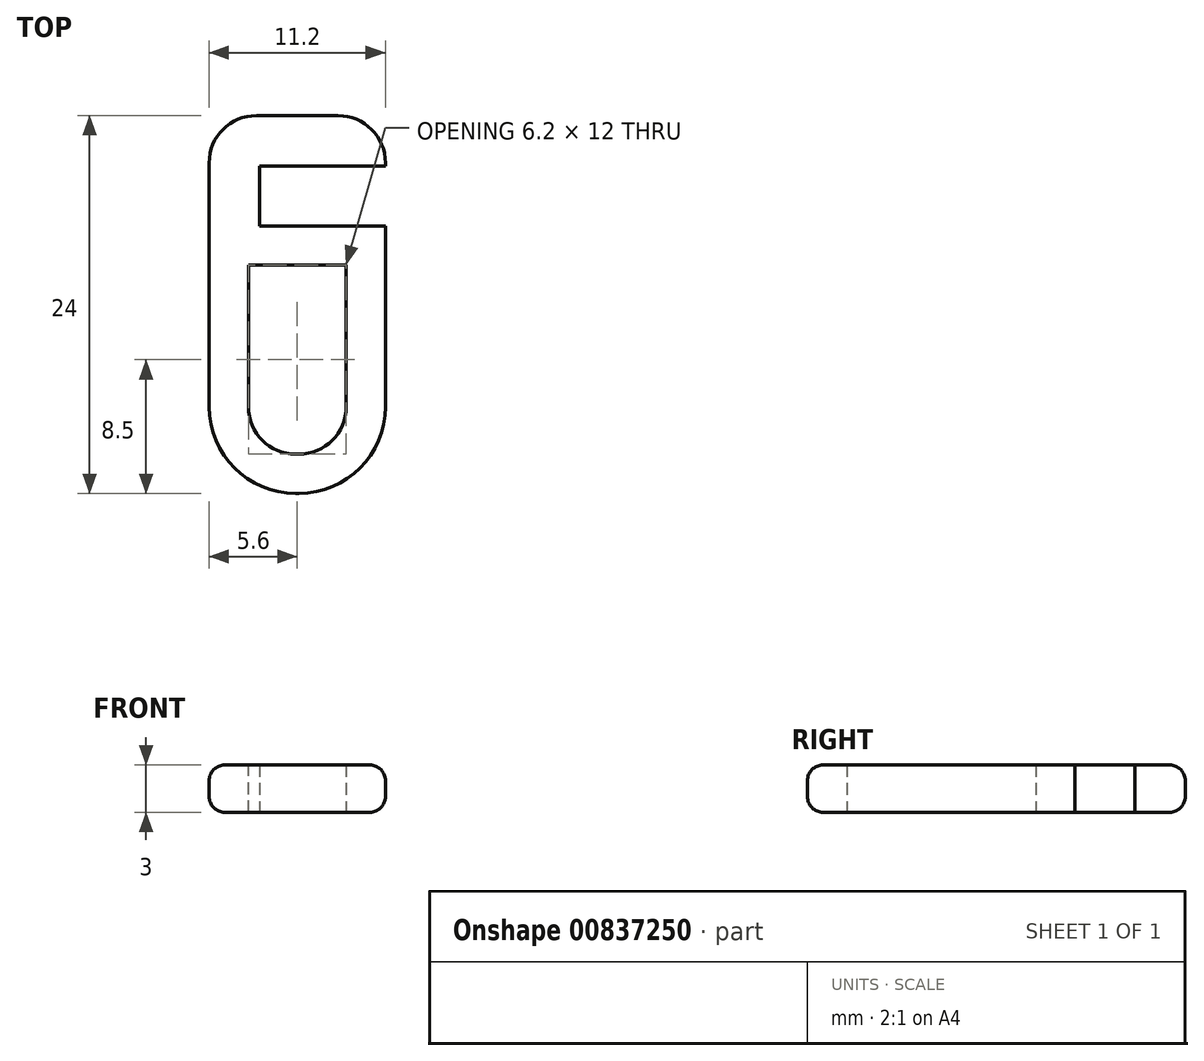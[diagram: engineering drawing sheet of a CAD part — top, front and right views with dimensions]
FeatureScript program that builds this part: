
annotation { "Feature Type Name" : "Feature", "Feature Type Description" : "" }
export const myFeature = defineFeature(function(context is Context, id is Id, definition is map)
    precondition{}
    {
        {
            var Q0;
            Q0=qCreatedBy(makeId("Top.planeOp"),FACE);
            var sketch = newSketch(context, id + "F0", { "sketchPlane" : qUnion([Q0])});
            skLineSegment(sketch, "E0", {"start": v(0, 0) * mm, "end": v(0, -17) * mm, "construction": true});
            skLineSegment(sketch, "E1", {"start": v(0, 0) * mm, "end": v(0, 3.8) * mm, "construction": true});
            skLineSegment(sketch, "E2", {"start": v(0, 18.8) * mm, "end": v(0, 3.8) * mm, "construction": true});
            skLineSegment(sketch, "E3", {"start": v(0, 0) * mm, "end": v(8, 0) * mm, "construction": true});
            skLineSegment(sketch, "E4.bottom", {"start": v(8, 0) * mm, "end": v(-3.2, 0) * mm});
            skLineSegment(sketch, "E4.top", {"start": v(8, -17) * mm, "end": v(-3.2, -17) * mm});
            skLineSegment(sketch, "E4.left", {"start": v(8, 0) * mm, "end": v(8, -17) * mm});
            skLineSegment(sketch, "E4.right", {"start": v(-3.2, 0) * mm, "end": v(-3.2, -17) * mm});
            skLineSegment(sketch, "E5.bottom", {"start": v(-3.2, 3.8) * mm, "end": v(0, 3.8) * mm});
            skLineSegment(sketch, "E5.top", {"start": v(-3.2, 0) * mm, "end": v(0, 0) * mm});
            skLineSegment(sketch, "E5.left", {"start": v(-3.2, 3.8) * mm, "end": v(-3.2, 0) * mm});
            skLineSegment(sketch, "E5.right", {"start": v(0, 3.8) * mm, "end": v(0, 0) * mm});
            skLineSegment(sketch, "E6.bottom", {"start": v(-3.2, 3.8) * mm, "end": v(8, 3.8) * mm});
            skLineSegment(sketch, "E6.top", {"start": v(-3.2, 7) * mm, "end": v(8, 7) * mm});
            skLineSegment(sketch, "E6.left", {"start": v(-3.2, 3.8) * mm, "end": v(-3.2, 7) * mm});
            skLineSegment(sketch, "E6.right", {"start": v(8, 3.8) * mm, "end": v(8, 7) * mm});
            skSolve(sketch);
        }
        {
            var Q0;
            Q0 = qSketchRegion(id + "F0", true);
            extrude(context, id + "F1", {"entities" : qUnion([Q0]), "depth" : 3 * mm, "offsetDistance" : 25 * mm});
        }
        {
            var Q0;
            Q0=makeQuery(id+"F1.opExtrude","SWEPT_EDGE",EDGE,{"disambiguationData":[OSD([sQuery(id+"F0.wireOp",EDGE,"E6.top"),sQuery(id+"F0.wireOp",EDGE,"E6.left")])]});
            var Q1;
            Q1=makeQuery(id+"F1.opExtrude","SWEPT_EDGE",EDGE,{"disambiguationData":[OSD([sQuery(id+"F0.wireOp",EDGE,"E6.top"),sQuery(id+"F0.wireOp",EDGE,"E6.right")])]});
            fillet(context, id + "F2", {"entities" : qUnion([Q0, Q1]), "radius" : 3 * mm, "tangentPropagation" : true, "allowEdgeOverflow" : false});
        }
        {
            var Q0;
            Q0=makeQuery(id+"F1.opExtrude","SWEPT_EDGE",EDGE,{"disambiguationData":[OSD([sQuery(id+"F0.wireOp",EDGE,"E4.top"),sQuery(id+"F0.wireOp",EDGE,"E4.right")])]});
            var Q1;
            Q1=makeQuery(id+"F1.opExtrude","SWEPT_EDGE",EDGE,{"disambiguationData":[OSD([sQuery(id+"F0.wireOp",EDGE,"E4.top"),sQuery(id+"F0.wireOp",EDGE,"E4.left")])]});
            fillet(context, id + "F3", {"entities" : qUnion([Q0, Q1]), "radius" : 5.5 * mm, "tangentPropagation" : true, "allowEdgeOverflow" : false});
        }
        {
            var Q0;
            Q0=makeQuery(id+"F1.opExtrude","SWEPT_FACE",FACE,{"disambiguationData":[OSD([sQuery(id+"F0.wireOp",EDGE,"E4.right"),sQuery(id+"F0.wireOp",EDGE,"E5.left"),sQuery(id+"F0.wireOp",EDGE,"E6.left")])]});
            fillet(context, id + "F4", {"entities" : qUnion([Q0]), "radius" : 1 * mm, "tangentPropagation" : true, "allowEdgeOverflow" : false});
        }
        {
            var Q0;
            Q0=makeQuery(id+"F1.opExtrude","CAP_FACE",FACE,{"disambiguationData":[OSD([sQuery(id+"F0.wireOp",EDGE,"E4.bottom"),sQuery(id+"F0.wireOp",EDGE,"E4.top"),sQuery(id+"F0.wireOp",EDGE,"E4.left"),sQuery(id+"F0.wireOp",EDGE,"E4.right"),sQuery(id+"F0.wireOp",EDGE,"E5.left"),sQuery(id+"F0.wireOp",EDGE,"E5.right"),sQuery(id+"F0.wireOp",EDGE,"E6.bottom"),sQuery(id+"F0.wireOp",EDGE,"E6.top"),sQuery(id+"F0.wireOp",EDGE,"E6.left"),sQuery(id+"F0.wireOp",EDGE,"E6.right")])],"isStart":false});
            var Q1;
            Q1=makeQuery(id+"F1.opExtrude","CAP_FACE",FACE,{"disambiguationData":[OSD([sQuery(id+"F0.wireOp",EDGE,"E4.bottom"),sQuery(id+"F0.wireOp",EDGE,"E4.top"),sQuery(id+"F0.wireOp",EDGE,"E4.left"),sQuery(id+"F0.wireOp",EDGE,"E4.right"),sQuery(id+"F0.wireOp",EDGE,"E5.left"),sQuery(id+"F0.wireOp",EDGE,"E5.right"),sQuery(id+"F0.wireOp",EDGE,"E6.bottom"),sQuery(id+"F0.wireOp",EDGE,"E6.top"),sQuery(id+"F0.wireOp",EDGE,"E6.left"),sQuery(id+"F0.wireOp",EDGE,"E6.right")])],"isStart":true});
            shell(context, id + "F5", {"entities" : qUnion([Q0, Q1]), "thickness" : 2.5 * mm});
        }
    });
